# Revit family: P190780JX-045c_JJW3830IL_Cooking_Wall-Oven
name_source: partatom
category: Specialty Equipment
units: mm (PartAtom-declared; Revit-internal decimal feet)

## family parameters
Always vertical = Yes
Cut with Voids When Loaded = No
Enable Cutting in Views = No
Maintain Annotation Orientation = No
Part Type = Normal
Room Calculation Point = No
Round Connector Dimension = Use Diameter
Shared = No
Work Plane-Based = No

## types (1)
- JJW3830IL
    Apparent Load = 0 VA
    Body Material = ARCAT - Metal - Steel - Stainless
    Clearance Material = ARCAT - Clearance
    Default Elevation = 0"
    Depth = 23 1/4"
    Description = RISE™ 30" Double Wall Oven with V2™ Vertical Dual-Fan Convection
Four mural simple RISE™ avec système de convection à deux ventilateurs verticaux V2™, 30 po
    Dimension Guide = http://access.whirlpool.com Guide&sku=JJW3830IL&language=EN
    Display Panel Material = ARCAT - Glass - Black
    Door Material = ARCAT - Metal - Steel - Stainless
    Family Name = DOUBLE WALL OVENS - 30"
    Feature 1 = Irresistible Interior
Intérieur irrésistible
    Feature 2 = 7-Inch Full Color LCD Display
Affichage en couleur ACL de 7 po
    Feature 3 = Cinematic Lighting
Éclairage cinématique
    Glass Material = ARCAT - Glass - Tempered - Black
    Handle Material = ARCAT - Metal - Steel - Gray
    Height = 52 3/8"
    Installation-Fabrication = http://access.whirlpool.com Instruction&sku=JJW3430IL&language=EN
    Manufacturer = Jenn Air
    Model = JJW3830IL
    Voltage = 0 V
    Width = 30"

## geometry (parser evidence)
native form markers: Sweep x3
no freeform markers — native parametric forms only
